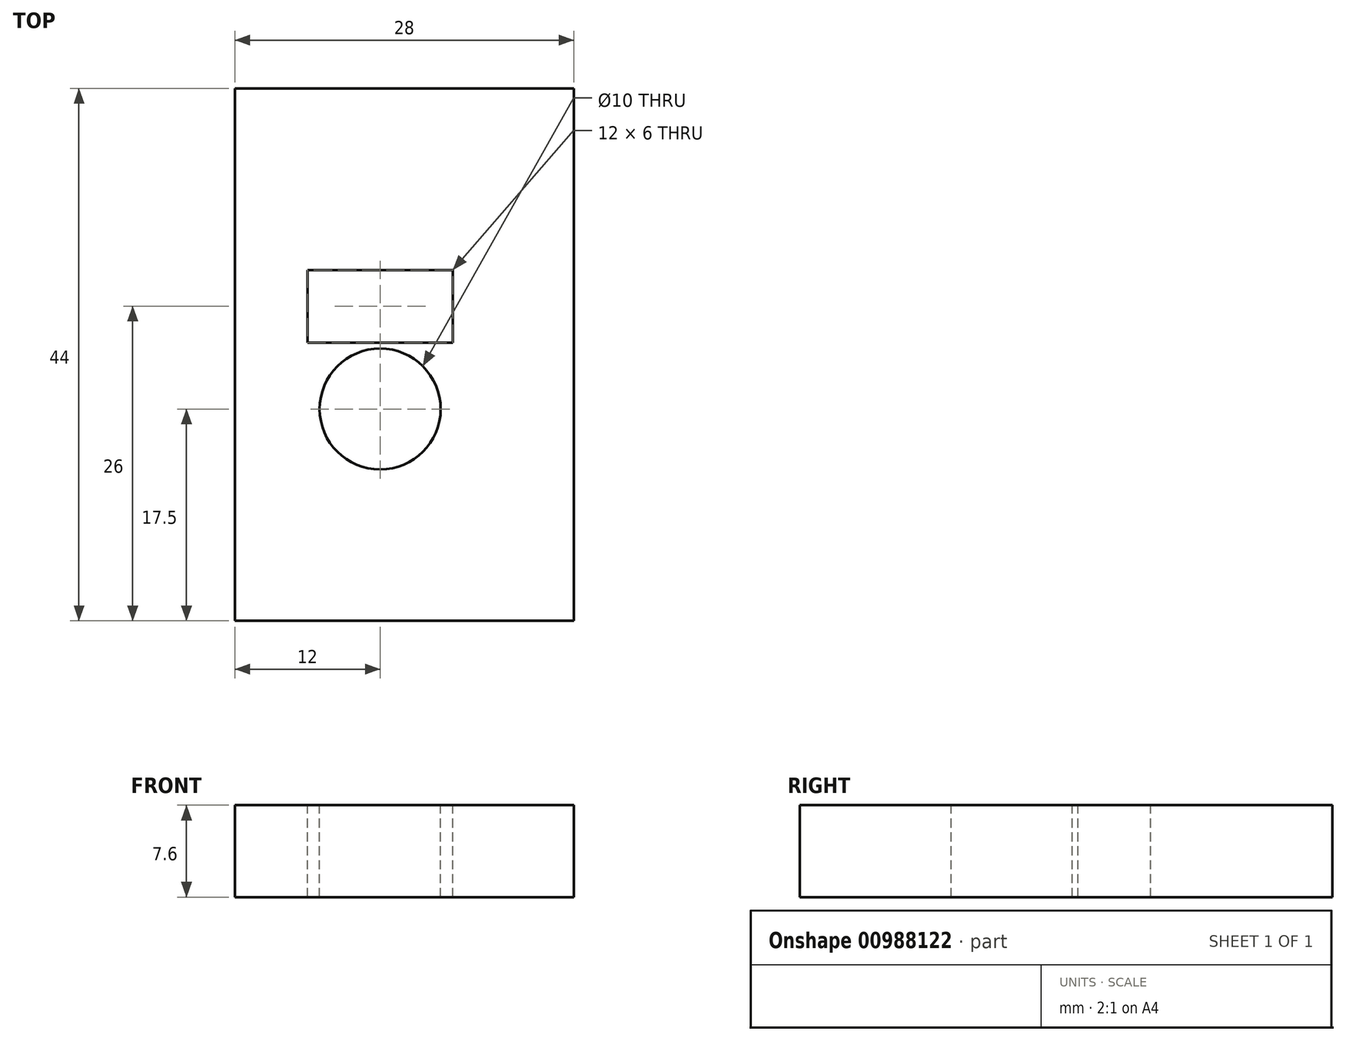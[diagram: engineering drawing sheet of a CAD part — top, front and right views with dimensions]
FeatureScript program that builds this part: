
annotation { "Feature Type Name" : "Feature", "Feature Type Description" : "" }
export const myFeature = defineFeature(function(context is Context, id is Id, definition is map)
    precondition{}
    {
        {
            var Q0;
            Q0=qCreatedBy(makeId("Top.planeOp"),FACE);
            var sketch = newSketch(context, id + "F0", { "sketchPlane" : qUnion([Q0])});
            skLineSegment(sketch, "E0.bottom", {"start": v(0, 0) * mm, "end": v(28, 0) * mm});
            skLineSegment(sketch, "E0.top", {"start": v(0, 44) * mm, "end": v(28, 44) * mm});
            skLineSegment(sketch, "E0.left", {"start": v(0, 0) * mm, "end": v(0, 44) * mm});
            skLineSegment(sketch, "E0.right", {"start": v(28, 0) * mm, "end": v(28, 44) * mm});
            skSolve(sketch);
        }
        {
            var Q0;
            Q0 = qSketchRegion(id + "F0", true);
            extrude(context, id + "F1", {"entities" : qUnion([Q0]), "depth" : 7.6 * mm, "offsetDistance" : 25 * mm});
        }
        {
            var Q0;
            Q0=makeQuery(id+"F1.opExtrude","CAP_FACE",FACE,{"disambiguationData":[OSD([sQuery(id+"F0.wireOp",EDGE,"E0.bottom"),sQuery(id+"F0.wireOp",EDGE,"E0.top"),sQuery(id+"F0.wireOp",EDGE,"E0.left"),sQuery(id+"F0.wireOp",EDGE,"E0.right")])],"isStart":false});
            var sketch = newSketch(context, id + "F2", { "sketchPlane" : qUnion([Q0])});
            skCircle(sketch, "E1", {"center": v(12, 17.5) * mm, "radius": 5 * mm});
            skLineSegment(sketch, "E2.bottom", {"start": v(6, 29) * mm, "end": v(18, 29) * mm});
            skLineSegment(sketch, "E2.top", {"start": v(6, 23) * mm, "end": v(18, 23) * mm});
            skLineSegment(sketch, "E2.left", {"start": v(6, 29) * mm, "end": v(6, 23) * mm});
            skLineSegment(sketch, "E2.right", {"start": v(18, 29) * mm, "end": v(18, 23) * mm});
            skSolve(sketch);
        }
        {
            var Q0;
            Q0 = qSketchRegion(id + "F2", true);
            extrude(context, id + "F3", {"entities" : qUnion([Q0]), "operationType" : NewBodyOperationType.REMOVE, "endBound" : BoundingType.THROUGH_ALL, "oppositeDirection" : true, "depth" : 25 * mm, "offsetDistance" : 25 * mm});
        }
    });
